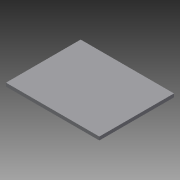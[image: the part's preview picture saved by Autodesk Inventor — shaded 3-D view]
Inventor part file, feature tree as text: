
AUTODESK INVENTOR PART (.ipt)
format: ipt  version: 2013 (Build 170138000, 138)  size: 65,536 bytes
history: native  units: mm
features: extrude x1, sketch x1
ambient origin geometry x8: Origin, YZ Plane, XZ Plane, XY Plane, X Axis, Y Axis, Z Axis, Center Point
bodies: Solid1 (feature_tree)
feature tree (2):
  extrude  "Extrusion1"  Depth=400.0mm
  sketch  "Sketch1"  dims[d0=500.0mm d2=400.0mm d3=18.0mm d4=0.0mm]
